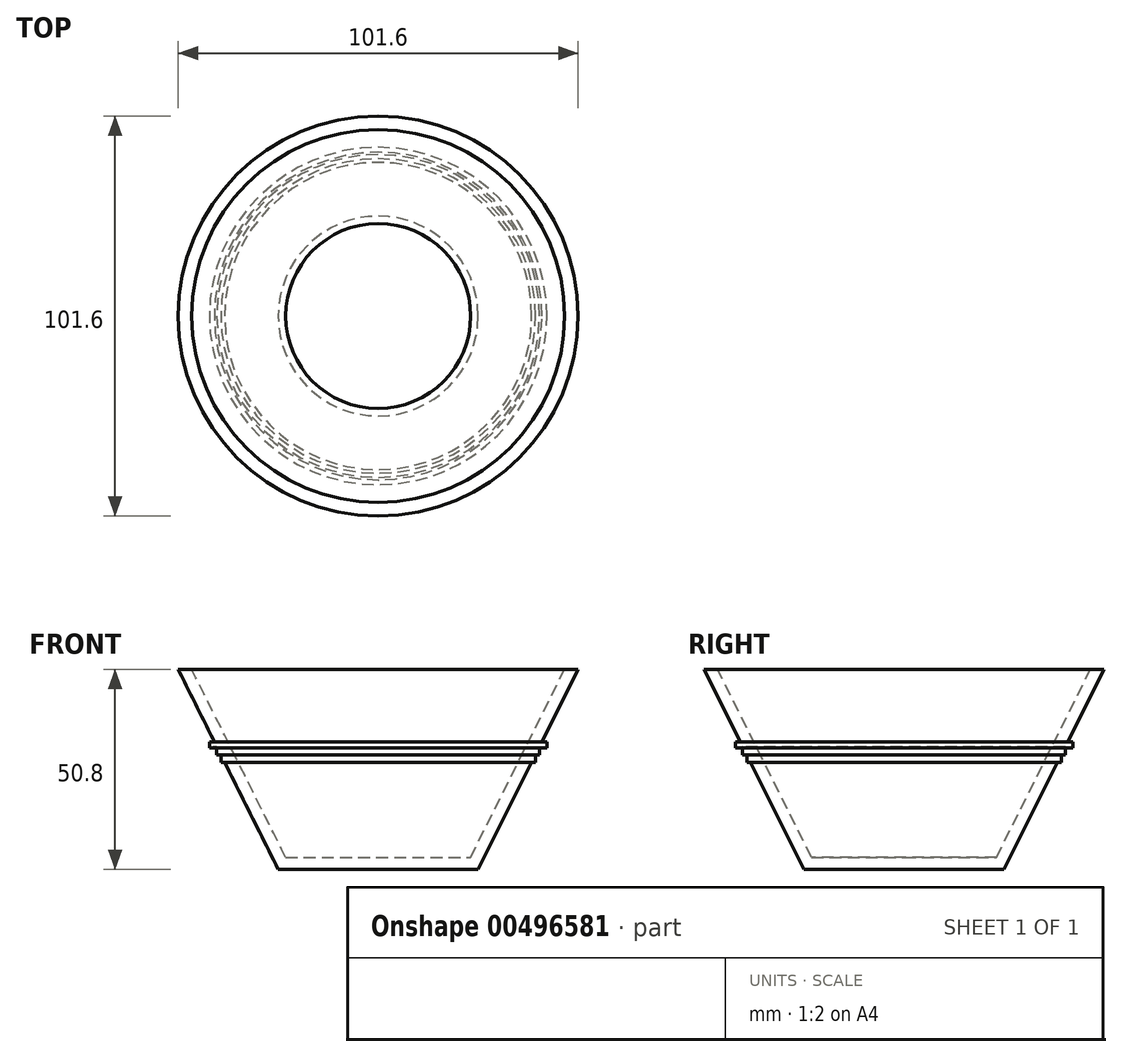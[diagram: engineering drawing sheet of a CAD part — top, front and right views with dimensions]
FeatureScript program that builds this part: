
annotation { "Feature Type Name" : "Feature", "Feature Type Description" : "" }
export const myFeature = defineFeature(function(context is Context, id is Id, definition is map)
    precondition{}
    {
        {
            var Q0;
            Q0=qCreatedBy(makeId("Front.planeOp"),FACE);
            var sketch = newSketch(context, id + "F0", { "sketchPlane" : qUnion([Q0])});
            skLineSegment(sketch, "E0", {"start": v(0, 0) * mm, "end": v(0, 50.8) * mm, "construction": true});
            skLineSegment(sketch, "E1", {"start": v(0, 0) * mm, "end": v(25.4, 0) * mm});
            skLineSegment(sketch, "E2", {"start": v(25.4, 0) * mm, "end": v(50.8, 50.8) * mm});
            skLineSegment(sketch, "E3.0", {"start": v(23.5, 3.07) * mm, "end": v(47.36, 50.8) * mm});
            skLineSegment(sketch, "E3.1", {"start": v(0, 3.07) * mm, "end": v(23.5, 3.07) * mm});
            skLineSegment(sketch, "E4", {"start": v(0, 3.07) * mm, "end": v(0, 0) * mm});
            skLineSegment(sketch, "E5", {"start": v(47.36, 50.8) * mm, "end": v(50.8, 50.8) * mm});
            skLineSegment(sketch, "E6", {"start": v(41.6, 32.42) * mm, "end": v(42.86, 32.42) * mm});
            skLineSegment(sketch, "E7", {"start": v(42.86, 32.42) * mm, "end": v(42.86, 30.93) * mm});
            skLineSegment(sketch, "E8", {"start": v(42.86, 30.93) * mm, "end": v(41, 31.19) * mm});
            skLineSegment(sketch, "E9", {"start": v(41, 31.19) * mm, "end": v(41, 29.11) * mm});
            skLineSegment(sketch, "E10", {"start": v(41, 29.11) * mm, "end": v(39.96, 29.11) * mm});
            skLineSegment(sketch, "E11", {"start": v(39.96, 29.11) * mm, "end": v(41, 29.11) * mm});
            skLineSegment(sketch, "E12", {"start": v(39.96, 27.24) * mm, "end": v(39.02, 27.24) * mm});
            skLineSegment(sketch, "E13", {"start": v(39.96, 27.24) * mm, "end": v(39.96, 29.11) * mm});
            skSolve(sketch);
        }
        {
            var Q0;
            Q0=makeQuery(id+"F0.imprint","IMPRINT",FACE,{"disambiguationData":[TD([[makeQuery(id+"F0.imprint","IMPRINT",EDGE,{"derivedFrom":sQuery(id+"F0.wireOp",EDGE,"E1")}),1.0]])]});
            var Q1;
            {var subQ0=sQuery(id+"F0.wireOp",EDGE,"E6");Q1=makeQuery(id+"F0.imprint","IMPRINT",FACE,{"disambiguationData":[TD([[makeQuery(id+"F0.imprint","IMPRINT",EDGE,{"derivedFrom":subQ0}),-1.0]])]});}
            var Q2;
            {var subQ0=sQuery(id+"F0.wireOp",EDGE,"E9");Q2=makeQuery(id+"F0.imprint","IMPRINT",FACE,{"disambiguationData":[TD([[makeQuery(id+"F0.imprint","IMPRINT",EDGE,{"derivedFrom":subQ0}),-1.0]])]});}
            var Q3;
            {var subQ2=sQuery(id+"F0.wireOp",EDGE,"E12");Q3=makeQuery(id+"F0.imprint","IMPRINT",FACE,{"disambiguationData":[TD([[makeQuery(id+"F0.imprint","IMPRINT",EDGE,{"derivedFrom":subQ2}),-1.0]])]});}
            var Q4;
            Q4=sQuery(id+"F0.wireOp",EDGE,"E0");
            revolve(context, id + "F1", {"entities" : qUnion([Q0, Q1, Q2, Q3]), "axis" : qUnion([Q4]), "revolveType" : RevolveType.FULL});
        }
    });
